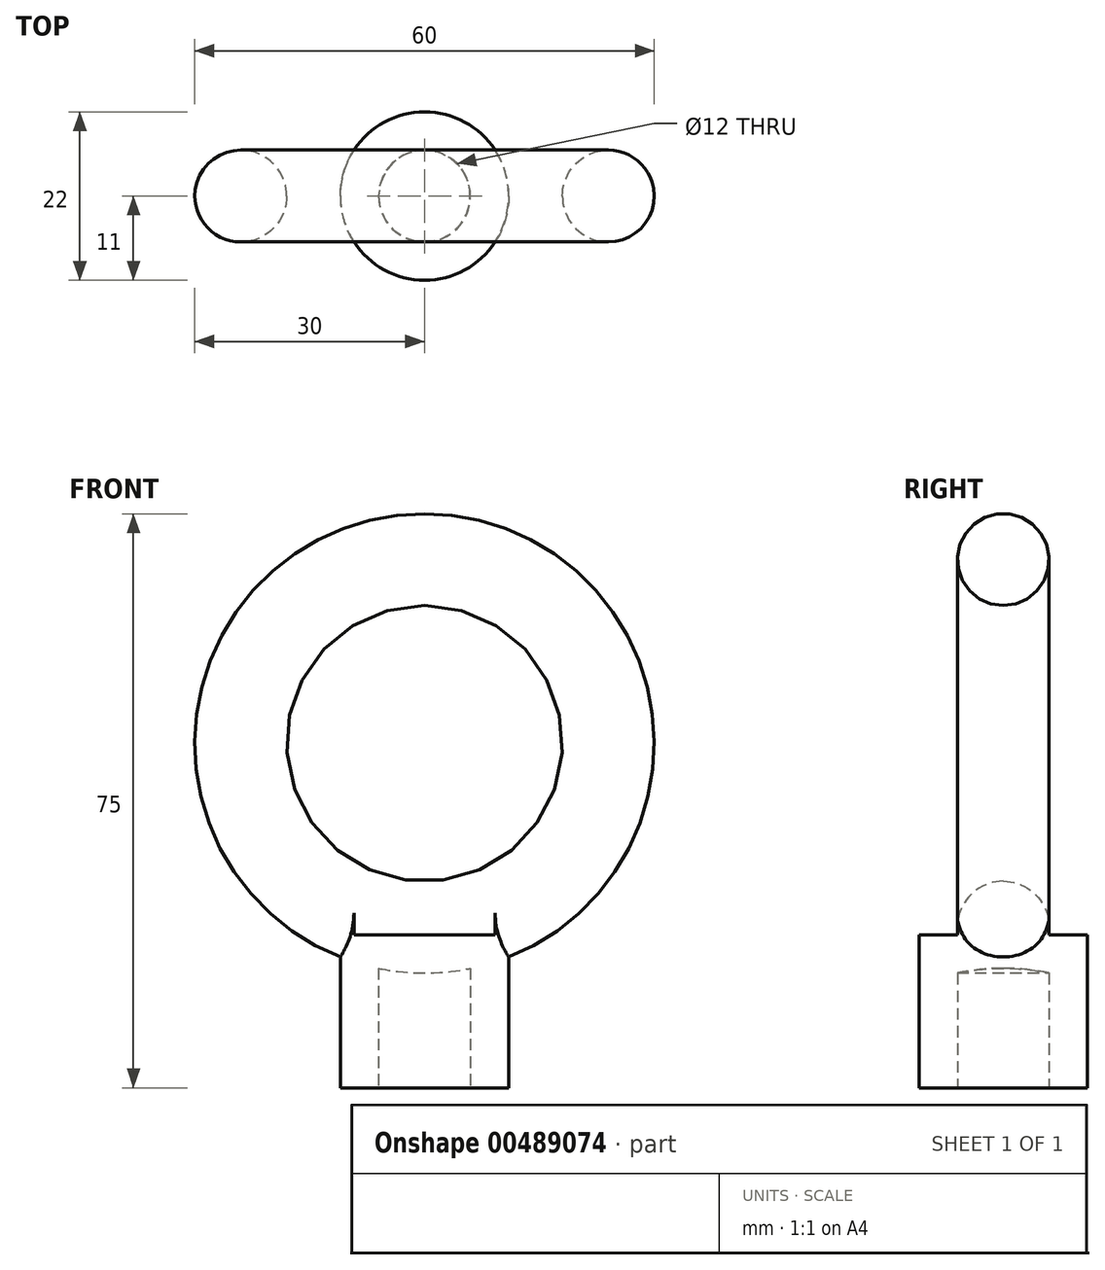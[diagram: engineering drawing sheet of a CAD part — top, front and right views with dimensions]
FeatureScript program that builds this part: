
annotation { "Feature Type Name" : "Feature", "Feature Type Description" : "" }
export const myFeature = defineFeature(function(context is Context, id is Id, definition is map)
    precondition{}
    {
        {
            var Q0;
            Q0=qCreatedBy(makeId("Top.planeOp"),FACE);
            var sketch = newSketch(context, id + "F0", { "sketchPlane" : qUnion([Q0])});
            skCircle(sketch, "E0", {"center": v(0, 0) * mm, "radius": 11 * mm});
            skCircle(sketch, "E1", {"center": v(0, 0) * mm, "radius": 6 * mm});
            skSolve(sketch);
        }
        {
            var Q0;
            Q0 = qSketchRegion(id + "F0", true);
            extrude(context, id + "F1", {"entities" : qUnion([Q0]), "depth" : 20 * mm});
        }
        {
            var Q0;
            Q0=qCreatedBy(makeId("Front.planeOp"),FACE);
            var sketch = newSketch(context, id + "F2", { "sketchPlane" : qUnion([Q0])});
            skCircle(sketch, "E2", {"center": v(0, 45) * mm, "radius": 30 * mm});
            skCircle(sketch, "E3", {"center": v(0, 45) * mm, "radius": 18 * mm});
            skSolve(sketch);
        }
        {
            var Q0;
            Q0 = qSketchRegion(id + "F2", true);
            extrude(context, id + "F3", {"entities" : qUnion([Q0]), "operationType" : NewBodyOperationType.ADD, "depth" : 12 * mm, "symmetric" : true});
        }
        {
            var Q0;
            Q0=makeQuery(id+"F3.opExtrude","CAP_EDGE",EDGE,{"disambiguationData":[OSD([sQuery(id+"F2.wireOp",EDGE,"E2")])],"isStart":false});
            var Q1;
            Q1=makeQuery(id+"F3.opExtrude","CAP_EDGE",EDGE,{"disambiguationData":[OSD([sQuery(id+"F2.wireOp",EDGE,"E3")])],"isStart":false});
            var Q2;
            Q2=makeQuery(id+"F3.opExtrude","CAP_EDGE",EDGE,{"disambiguationData":[OSD([sQuery(id+"F2.wireOp",EDGE,"E2")])],"isStart":true});
            var Q3;
            Q3=makeQuery(id+"F3.opExtrude","CAP_EDGE",EDGE,{"disambiguationData":[OSD([sQuery(id+"F2.wireOp",EDGE,"E3")])],"isStart":true});
            fillet(context, id + "F4", {"entities" : qUnion([Q0, Q1, Q2, Q3]), "radius" : 6 * mm, "tangentPropagation" : true, "allowEdgeOverflow" : false});
        }
    });
